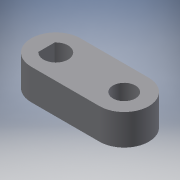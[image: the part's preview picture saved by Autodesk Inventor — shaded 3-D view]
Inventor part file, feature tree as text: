
AUTODESK INVENTOR PART (.ipt)
format: ipt  version: 2017 (Build 210142000, 142)  size: 110,080 bytes
history: native  units: mm
features: extrude x2, sketch x2
ambient origin geometry x8: Origin, YZ Plane, XZ Plane, XY Plane, X Axis, Y Axis, Z Axis, Center Point
bodies: Solid1 (feature_tree)
feature tree (4):
  extrude  "Extrusion1"  Depth=8.0mm
  extrude  "Extrusion2"  Depth=16.0mm
  sketch  "Sketch1"  dims[d0=22.225mm d1=8.0mm]
  sketch  "Sketch2"  dims[d2=7.3mm d3=16.0mm d4=10.0mm d5=0.0mm d6=7.0mm d7=12.0mm d8=0.0mm]
